# Revit family: QF_Marco_1000859
name_source: partatom
category: Specialty Equipment
units: mm (PartAtom-declared; Revit-internal decimal feet)

## family parameters
Always vertical = Yes
Cut with Voids When Loaded = No
Part Type = Normal
Room Calculation Point = No
Round Connector Dimension = Use Diameter
Shared = No
Work Plane-Based = No

## types (1)
- QF_Marco_1000859
    Apparent Power = 0 VA
    Cold Water Connection Height = 0 "
    Cold Water Flow = 0 GPM
    Cold Water Maximum Pressure = 0.00 psi
    Cold Water Minimum Pressure = 0.00 psi
    Cold Water RI Height = 0 "
    Cold Water Size = 0"
    Cold Water Temperature Recommended = 0 °F
    Conn Conduit = Yes
    Conn Plug = NEMA L6-20P
    Cycle = 60 Hz
    Depth = 5.433 "
    Description = Una Font - 247mm High
    Elec Conn Connection Height = 0 "
    Elec Conn RI Height = 0 "
    FL Amps = 0 A
    Foodservice Equipment Identifier = Yes
    Height = 9.724 "
    Hot Water Connection Height = 0 "
    Hot Water Consumption = 0 GPM
    Hot Water Flow = 0 GPM
    Hot Water Maximum Pressure = 0.00 psi
    Hot Water Minimum Pressure = 0.00 psi
    Hot Water RI Height = 0 "
    Hot Water Size = 0"
    Hot Water Temperature = 0 °F
    Identify Quantity as Lot = Yes
    Length = 1.181 "
    Manufacturer = Marco
    Max Overcurrent Protection = 0 A
    Min Ckt Ampacity = 0 A
    Model = 1000859
    Number of Poles = 1
    Phase = 1
    Volts = 0 V
    Watts = 0 W
    Weight in Pounds = 21

## geometry (parser evidence)
native form markers: Sweep x4
no freeform markers — native parametric forms only
